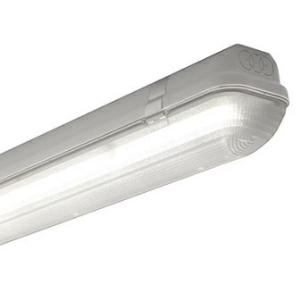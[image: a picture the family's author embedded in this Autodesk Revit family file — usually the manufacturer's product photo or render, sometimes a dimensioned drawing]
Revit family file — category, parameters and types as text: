
# Revit family: 3f_filippi_-_3f_linda_3f_filippi_-_58605_-_3f_linda_led_1x30w_l1570
name_source: partatom
category: Lighting Fixtures
units: mm (PartAtom-declared; Revit-internal decimal feet)

## family parameters
Cut with Voids When Loaded = No
Host = Face
Light Source = No
Part Type = Normal
Room Calculation Point = No
Round Connector Dimension = Use Diameter
Shared = No

## types (1)
- 3F Filippi - 3F Linda (1 x LED, 5180 lm, 33.5 W, 4000 K)
    Apparent Load = 34 VA
    Approval mark = CE
    CIE Flux Codes = 44 77 94 97 100
    Color Rendering = 80
    Color Temperature = 4000 K
    Control Gear = Electronic ballast
    Default Elevation = 1800 mm
    Description = ILLUMINOTECHNICAL
Luminous efficiency 100% (DLOR 97%, ULOR 3%).
Initial luminous flux of the luminaire 5180 lm.
Controlled symmetric distribution.
Installation Interdistance Transv.D = 1.77 x hu - Long.D = 1.17 x hu.
Tabular UGR (CIE 117 - 4H-8H; S=0.25H; 70/50/20): RUG 22.1 - 23.1.
Beam angle: 109° - 64°.
Luminous efficacy 155 lm/W.
Lifetime (L93/B10): 30000 h. (tq+25°C)
Lifetime (L90/B10): 50000 h. (tq+25°C)
Lifetime (L85/B10): 80000 h. (tq+25°C)
Lifetime (L80/B10): 100000 h. (tq+25°C)
Lifetime (L85/B10): 50000 h. (tq+35°C)
Sudden decreased luminous flux after 50000 hours: 0% (C0).
Photobiological safety in compliance with IEC/TR 62778: RG0 risk exempt, (IEC 62471).
In compliance with IEC/EN 62722-2-1 - IEC/EN 62717 standards.

SOURCE
Linear LED module 30W/840.
Energy efficiency class (UE 2019/2020 - UE 2019/2015): D.
CIE 13.3 Colour rendering index: CRI >80 (R9 <50%).
IES TM-30 Fidelity Index: Rf = 84 Rg = 95.
CCT nominal colour temperature 4000 K.
Colour initial tolerance (MacAdam): SDCM 3.

MECHANICAL
Self-extinguishing V2 polycarbonate housing, injection moulded, RAL 7035 grey.
Ecologic anti-aging injected sealing gasket.
Diffuser in self-extinguishing V2 polycarbonate, photo-engraved interior, UV stabilised, injection moulded with smooth outer surface, tamper-proof opening.
Gear-holder reflector in hot-dip galvanised steel, painted with white polyester base.
Snug fit safety snap-lock clips for diffuser mounting in stainless steel, screwdriver opening.
Fixing brackets in stainless steel.
Possibility for technicians to access the interior of the luminaire.
Luminaire with limited surface temperature. - D - (EN 60598-2-24)
Dimensions: 1570x100 mm, height 100 mm. Weight 2.5 kg.
IP66 protection degree.
Mechanical strength to impacts IK10 (20 joule).
Glow-wire test resistance 850°C.

ELECTRICAL
Halogen Free electronic wiring 230V-50/60Hz, power factor 0.95, THD <25%, constant output current, SELV, class I, 1 driver.
Power of the luminaire 33.5 W.
ENEC - CE.
SAFE FLICKER: PstLM=<1 and SVM=<0.4 (IEC TR 61547-1 and IEC TR 63158), to ensure a more comfortable and safe light.
Luminaire compliant with EN 60598-2-22 for power supply from a centralised emergency system CPSS (Central Power Supply System), not incorporated in the luminaire - high risk areas excluded. The default power and flux are 100% in AC and 100% in DC.
Ambient temperature from -20°C to +35°C.
Temperature class T6 max 85°C.
Relative humidity UR: <85%.

INSTALLATION
Ceiling / Suspended / Wall.
All accessories dedicated to this product are available on the Catalog and on our website www.3F-Filippi.com.

APPLICATIONS
Suitable product for food production plants (HACCP), IFS (Food Version 6), BRC (GSFS Food Version 7).
Dry, dusty indoor environments, subject to occasional water splashes.
Virtually shatterproof polycarbonate compatibly with the fumes / atmospheres that compromise the elasticity of plastic materials.
Not suitable for installation on surfaces subject to important vibrations, exposed to weather conditions, on ropes or poles.
Suitable for illumination of public car parks and parking grounds referred to DIN 67528:2018-04.

WARNING
Fixture not suitable for cold stores with an ambient temperature <0°C and/or relative humidity >85%.
Luminaire designed for disposal/recycling at end-of-life.
Replaceable (LED only) light source by a professional. Replaceable control gear by a professional.
    Height = 100 mm  [stored 0.328084 ft]
    Lamp = 1 x LED
    Lamp Light Flux = 5180 lm
    Lamp Power = 33.5 W
    Lamp count = 1
    Length = 1570 mm
    Lifetime = 50000 h
    Luminous efficacy = 155 lm/W
    Manufacturer = 3F Filippi
    ModVariant = No
    Model = 3F Filippi - 58605 - 3F Linda LED 1x30W L1570
    Mounting Place = Ceiling
    Mounting Type = Pendant
    Number of Poles = 1
    OnlyDefault = Yes
    Power Factor = 1
    Product Name = 3F Filippi - 3F Linda
    Product group = pendant luminaire
    ProductGroupID = 9
    Protection Class = Protection class I
    Protection Degree = IP 66
    RLX_Detail_Level = 1
    RLX_Emergency_Light_Flux = 0 lm
    RLX_Emergency_Type = 0
    RLX_Emergency_Type_DB = No
    RlxData = <blob elided: 69557 chars, md5=37cde481>
    Socket = socket
    Standby Power = 0 W
    System Light Flux = 5180 lm
    System Power = 34 W
    Type Comments = Product without accessories
    Type Image = 3ffilippi_3f_linda_led_1x.jpg
    URL = http://relux.com
    VarID = ---
    Voltage = 0 V
    Weight = 0.00 kg
    Width = 100 mm  [stored 0.328084 ft]

note: [stored X ft] marks values corroborated as IEEE doubles in the binary element streams (Revit-internal decimal feet)

## geometry (parser evidence)
native form markers: Blend x4, Sweep x10
no freeform markers — native parametric forms only
